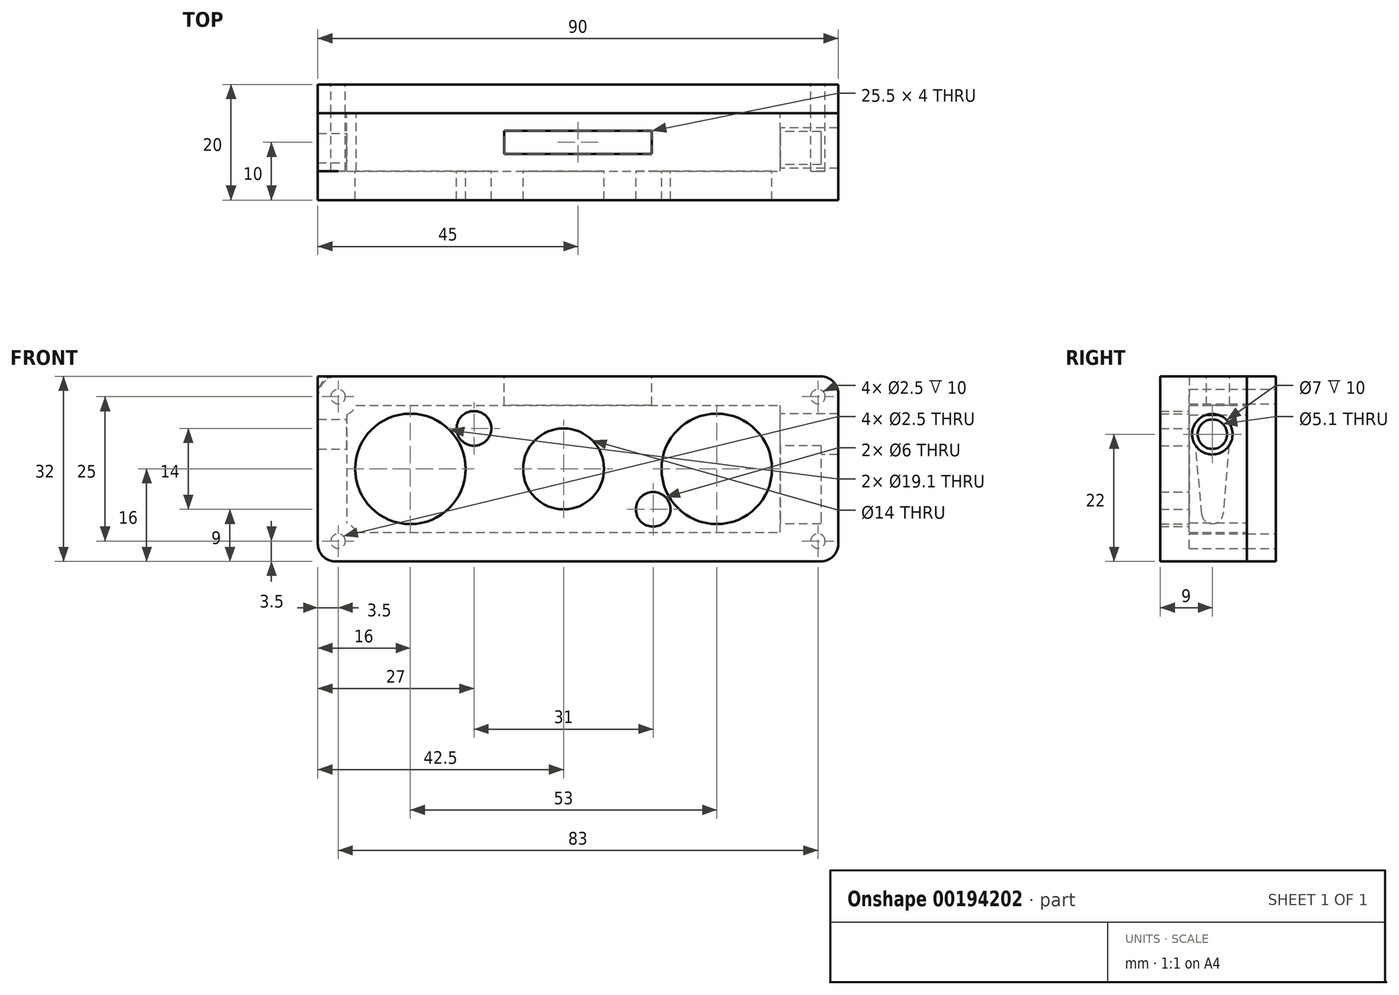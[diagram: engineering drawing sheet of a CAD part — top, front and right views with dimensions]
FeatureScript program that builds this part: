
annotation { "Feature Type Name" : "Feature", "Feature Type Description" : "" }
export const myFeature = defineFeature(function(context is Context, id is Id, definition is map)
    precondition{}
    {
        {
            var Q0;
            Q0=qCreatedBy(makeId("Front.planeOp"),FACE);
            var sketch = newSketch(context, id + "F0", { "sketchPlane" : qUnion([Q0])});
            skLineSegment(sketch, "E0.bottom", {"start": v(42.5, 16) * mm, "end": v(-42.5, 16) * mm});
            skLineSegment(sketch, "E0.top", {"start": v(42.5, -16) * mm, "end": v(-42.5, -16) * mm});
            skLineSegment(sketch, "E0.right", {"start": v(-42.5, 16) * mm, "end": v(-42.5, -16) * mm});
            skPoint(sketch, "E0.middle", {"position": v(0, 0) * mm});
            skCircle(sketch, "E1", {"center": v(-39, 12.5) * mm, "radius": 1.25 * mm});
            skCircle(sketch, "E2", {"center": v(-39, -12.5) * mm, "radius": 1.25 * mm});
            skCircle(sketch, "E3", {"center": v(44, 12.5) * mm, "radius": 1.25 * mm});
            skCircle(sketch, "E4", {"center": v(44, -12.5) * mm, "radius": 1.25 * mm});
            skLineSegment(sketch, "E5.bottom", {"start": v(42.5, 16) * mm, "end": v(47.5, 16) * mm});
            skLineSegment(sketch, "E5.top", {"start": v(42.5, -16) * mm, "end": v(47.5, -16) * mm});
            skLineSegment(sketch, "E5.right", {"start": v(47.5, 16) * mm, "end": v(47.5, -16) * mm});
            skSolve(sketch);
        }
        {
            var Q0;
            Q0=makeQuery(id+"F0.imprint","IMPRINT",FACE,{"disambiguationData":[TD([[makeQuery(id+"F0.imprint","IMPRINT",EDGE,{"derivedFrom":sQuery(id+"F0.wireOp",EDGE,"E0.bottom")}),1.0]])]});
            extrude(context, id + "F1", {"entities" : qUnion([Q0]), "depth" : 5 * mm});
        }
        {
            var Q0;
            Q0=makeQuery(id+"F1.opExtrude","CAP_FACE",FACE,{"disambiguationData":[OSD([sQuery(id+"F0.wireOp",EDGE,"E0.bottom"),sQuery(id+"F0.wireOp",EDGE,"E0.top"),sQuery(id+"F0.wireOp",EDGE,"E0.left"),sQuery(id+"F0.wireOp",EDGE,"E0.right"),sQuery(id+"F0.wireOp",EDGE,"E1"),sQuery(id+"F0.wireOp",EDGE,"E2"),sQuery(id+"F0.wireOp",EDGE,"E3"),sQuery(id+"F0.wireOp",EDGE,"E4")])],"isStart":false});
            var sketch = newSketch(context, id + "F2", { "sketchPlane" : qUnion([Q0])});
            skLineSegment(sketch, "E6.bottom", {"start": v(-42.5, 16) * mm, "end": v(42.5, 16) * mm});
            skLineSegment(sketch, "E6.top", {"start": v(-42.5, -16) * mm, "end": v(42.5, -16) * mm});
            skLineSegment(sketch, "E6.left", {"start": v(-42.5, 16) * mm, "end": v(-42.5, -16) * mm});
            skPoint(sketch, "E6.middle", {"position": v(0, 0) * mm});
            skLineSegment(sketch, "E7.bottom", {"start": v(-37.5, 11) * mm, "end": v(37.5, 11) * mm});
            skLineSegment(sketch, "E7.top", {"start": v(-37.5, -11) * mm, "end": v(37.5, -11) * mm});
            skLineSegment(sketch, "E7.left", {"start": v(-37.5, 11) * mm, "end": v(-37.5, -11) * mm});
            skCircle(sketch, "E8", {"center": v(-39, 12.5) * mm, "radius": 3.5 * mm});
            skCircle(sketch, "E9", {"center": v(-39, -12.5) * mm, "radius": 3.5 * mm});
            skCircle(sketch, "E10", {"center": v(-39, 12.5) * mm, "radius": 1.25 * mm});
            skCircle(sketch, "E11", {"center": v(-39, -12.5) * mm, "radius": 1.25 * mm});
            skCircle(sketch, "E12", {"center": v(44, -12.5) * mm, "radius": 1.25 * mm});
            skCircle(sketch, "E13", {"center": v(44, 12.5) * mm, "radius": 1.25 * mm});
            skLineSegment(sketch, "E14.bottom", {"start": v(47.5, 16) * mm, "end": v(42.5, 16) * mm});
            skLineSegment(sketch, "E14.top", {"start": v(47.5, -16) * mm, "end": v(42.5, -16) * mm});
            skLineSegment(sketch, "E14.left", {"start": v(47.5, 16) * mm, "end": v(47.5, -16) * mm});
            skLineSegment(sketch, "E15", {"start": v(37.5, -11) * mm, "end": v(37.5, 11) * mm});
            skSolve(sketch);
        }
        {
            var Q0;
            {var subQ0=sQuery(id+"F2.wireOp",EDGE,"E8");var subQ1=sQuery(id+"F2.wireOp",EDGE,"E6.left");var subQ2=makeQuery(id+"F2.imprint","INTERSECT",VERTEX,{"derivedFrom":[subQ1,subQ0]});Q0=makeQuery(id+"F2.imprint","IMPRINT",FACE,{"disambiguationData":[TD([[makeQuery(id+"F2.imprint","IMPRINT",EDGE,{"disambiguationData":[TD([[subQ2,-1.0]])],"derivedFrom":subQ1}),1.0]])]});}
            var Q1;
            Q1=makeQuery(id+"F2.imprint","IMPRINT",FACE,{"disambiguationData":[TD([[makeQuery(id+"F2.imprint","IMPRINT",EDGE,{"derivedFrom":sQuery(id+"F2.wireOp",EDGE,"E10")}),-1.0]])]});
            var Q2;
            {var subQ0=sQuery(id+"F2.wireOp",EDGE,"E6.left");var subQ1=sQuery(id+"F2.wireOp",EDGE,"E6.bottom");var subQ2=makeQuery(id+"F2.imprint","INTERSECT",VERTEX,{"derivedFrom":[subQ1,subQ0]});Q2=makeQuery(id+"F2.imprint","IMPRINT",FACE,{"disambiguationData":[TD([[makeQuery(id+"F2.imprint","IMPRINT",EDGE,{"disambiguationData":[TD([[subQ2,-1.0]])],"derivedFrom":subQ1}),-1.0]])]});}
            var Q3;
            {var subQ0=sQuery(id+"F2.wireOp",EDGE,"E6.left");var subQ1=sQuery(id+"F2.wireOp",EDGE,"E6.top");var subQ2=makeQuery(id+"F2.imprint","INTERSECT",VERTEX,{"derivedFrom":[subQ1,subQ0]});Q3=makeQuery(id+"F2.imprint","IMPRINT",FACE,{"disambiguationData":[TD([[makeQuery(id+"F2.imprint","IMPRINT",EDGE,{"disambiguationData":[TD([[subQ2,1.0]])],"derivedFrom":subQ1}),-1.0]])]});}
            var Q4;
            Q4=makeQuery(id+"F2.imprint","IMPRINT",FACE,{"disambiguationData":[TD([[makeQuery(id+"F2.imprint","IMPRINT",EDGE,{"derivedFrom":sQuery(id+"F2.wireOp",EDGE,"E11")}),-1.0]])]});
            var Q5;
            {var subQ3=sQuery(id+"F2.wireOp",EDGE,"E7.top");var subQ5=sQuery(id+"F2.wireOp",EDGE,"GZhXrjCj-0FAN-kLtT-mxsU-Lzp2gtZjm1nU.top");var subQ11=makeQuery(id+"F2.imprint","INTERSECT",VERTEX,{"derivedFrom":[subQ3,subQ5]});Q5=makeQuery(id+"F2.imprint","IMPRINT",FACE,{"disambiguationData":[TD([[makeQuery(id+"F2.imprint","IMPRINT",EDGE,{"disambiguationData":[TD([[subQ11,1.0]])],"derivedFrom":subQ3}),-1.0]])]});}
            var Q6;
            {var subQ0=sQuery(id+"F2.wireOp",EDGE,"GZhXrjCj-0FAN-kLtT-mxsU-Lzp2gtZjm1nU.top");var subQ1=sQuery(id+"F2.wireOp",EDGE,"AdWPE1ED-Ojqk-Ucqv-Uyvc-EErXh61Z168s");var subQ2=makeQuery(id+"F2.imprint","INTERSECT",VERTEX,{"derivedFrom":[subQ1,subQ0]});Q6=makeQuery(id+"F2.imprint","IMPRINT",FACE,{"disambiguationData":[TD([[makeQuery(id+"F2.imprint","IMPRINT",EDGE,{"disambiguationData":[TD([[subQ2,-1.0]])],"derivedFrom":subQ1}),1.0]])]});}
            var Q7;
            {var subQ0=sQuery(id+"F2.wireOp",EDGE,"GZhXrjCj-0FAN-kLtT-mxsU-Lzp2gtZjm1nU.right");var subQ1=sQuery(id+"F2.wireOp",EDGE,"AdWPE1ED-Ojqk-Ucqv-Uyvc-EErXh61Z168s");var subQ2=makeQuery(id+"F2.imprint","INTERSECT",VERTEX,{"derivedFrom":[subQ1,subQ0]});Q7=makeQuery(id+"F2.imprint","IMPRINT",FACE,{"disambiguationData":[TD([[makeQuery(id+"F2.imprint","IMPRINT",EDGE,{"disambiguationData":[TD([[subQ2,-1.0]])],"derivedFrom":subQ1}),1.0]])]});}
            var Q8;
            Q8=makeQuery(id+"F2.imprint","IMPRINT",FACE,{"disambiguationData":[TD([[makeQuery(id+"F2.imprint","IMPRINT",EDGE,{"derivedFrom":sQuery(id+"F2.wireOp",EDGE,"E12")}),-1.0]])]});
            var Q9;
            {var subQ0=sQuery(id+"F2.wireOp",EDGE,"E14.left");var subQ1=sQuery(id+"F2.wireOp",EDGE,"AdWPE1ED-Ojqk-Ucqv-Uyvc-EErXh61Z168s");var subQ2=makeQuery(id+"F2.imprint","INTERSECT",VERTEX,{"derivedFrom":[subQ1,subQ0]});Q9=makeQuery(id+"F2.imprint","IMPRINT",FACE,{"disambiguationData":[TD([[makeQuery(id+"F2.imprint","IMPRINT",EDGE,{"disambiguationData":[TD([[subQ2,1.0]])],"derivedFrom":subQ1}),-1.0]])]});}
            var Q10;
            {var subQ0=sQuery(id+"F2.wireOp",EDGE,"E14.top");var subQ1=sQuery(id+"F2.wireOp",EDGE,"AdWPE1ED-Ojqk-Ucqv-Uyvc-EErXh61Z168s");var subQ2=makeQuery(id+"F2.imprint","INTERSECT",VERTEX,{"derivedFrom":[subQ1,subQ0]});Q10=makeQuery(id+"F2.imprint","IMPRINT",FACE,{"disambiguationData":[TD([[makeQuery(id+"F2.imprint","IMPRINT",EDGE,{"disambiguationData":[TD([[subQ2,1.0]])],"derivedFrom":subQ1}),-1.0]])]});}
            var Q11;
            {var subQ0=sQuery(id+"F2.wireOp",EDGE,"E14.left");var subQ1=sQuery(id+"F2.wireOp",EDGE,"AdWPE1ED-Ojqk-Ucqv-Uyvc-EErXh61Z168s");var subQ2=makeQuery(id+"F2.imprint","INTERSECT",VERTEX,{"derivedFrom":[subQ1,subQ0]});Q11=makeQuery(id+"F2.imprint","IMPRINT",FACE,{"disambiguationData":[TD([[makeQuery(id+"F2.imprint","IMPRINT",EDGE,{"disambiguationData":[TD([[subQ2,-1.0]])],"derivedFrom":subQ1}),-1.0]])]});}
            var Q12;
            Q12=makeQuery(id+"F2.imprint","IMPRINT",FACE,{"disambiguationData":[TD([[makeQuery(id+"F2.imprint","IMPRINT",EDGE,{"derivedFrom":sQuery(id+"F2.wireOp",EDGE,"E13")}),-1.0]])]});
            var Q13;
            {var subQ0=sQuery(id+"F2.wireOp",EDGE,"E14.bottom");var subQ1=sQuery(id+"F2.wireOp",EDGE,"1qeEdO3c-cVBC-DGRz-gu55-AesEKtjOA0Mx");var subQ2=makeQuery(id+"F2.imprint","INTERSECT",VERTEX,{"derivedFrom":[subQ1,subQ0]});Q13=makeQuery(id+"F2.imprint","IMPRINT",FACE,{"disambiguationData":[TD([[makeQuery(id+"F2.imprint","IMPRINT",EDGE,{"disambiguationData":[TD([[subQ2,1.0]])],"derivedFrom":subQ1}),-1.0]])]});}
            var Q14;
            {var subQ0=sQuery(id+"F2.wireOp",EDGE,"E14.right");var subQ1=sQuery(id+"F2.wireOp",EDGE,"1qeEdO3c-cVBC-DGRz-gu55-AesEKtjOA0Mx");var subQ2=makeQuery(id+"F2.imprint","INTERSECT",VERTEX,{"derivedFrom":[subQ1,subQ0]});Q14=makeQuery(id+"F2.imprint","IMPRINT",FACE,{"disambiguationData":[TD([[makeQuery(id+"F2.imprint","IMPRINT",EDGE,{"disambiguationData":[TD([[subQ2,-1.0]])],"derivedFrom":subQ1}),1.0]])]});}
            var Q15;
            {var subQ0=sQuery(id+"F2.wireOp",EDGE,"GZhXrjCj-0FAN-kLtT-mxsU-Lzp2gtZjm1nU.bottom");var subQ1=sQuery(id+"F2.wireOp",EDGE,"1qeEdO3c-cVBC-DGRz-gu55-AesEKtjOA0Mx");var subQ2=makeQuery(id+"F2.imprint","INTERSECT",VERTEX,{"derivedFrom":[subQ1,subQ0]});Q15=makeQuery(id+"F2.imprint","IMPRINT",FACE,{"disambiguationData":[TD([[makeQuery(id+"F2.imprint","IMPRINT",EDGE,{"disambiguationData":[TD([[subQ2,-1.0]])],"derivedFrom":subQ1}),1.0]])]});}
            var Q16;
            {var subQ3=sQuery(id+"F2.wireOp",EDGE,"GZhXrjCj-0FAN-kLtT-mxsU-Lzp2gtZjm1nU.bottom");var subQ9=sQuery(id+"F2.wireOp",EDGE,"E7.bottom");var subQ11=makeQuery(id+"F2.imprint","INTERSECT",VERTEX,{"derivedFrom":[subQ9,subQ3]});Q16=makeQuery(id+"F2.imprint","IMPRINT",FACE,{"disambiguationData":[TD([[makeQuery(id+"F2.imprint","IMPRINT",EDGE,{"disambiguationData":[TD([[subQ11,1.0]])],"derivedFrom":subQ9}),1.0]])]});}
            var Q17;
            {var subQ0=sQuery(id+"F2.wireOp",EDGE,"E14.bottom");var subQ1=sQuery(id+"F2.wireOp",EDGE,"1qeEdO3c-cVBC-DGRz-gu55-AesEKtjOA0Mx");var subQ2=makeQuery(id+"F2.imprint","INTERSECT",VERTEX,{"derivedFrom":[subQ1,subQ0]});Q17=makeQuery(id+"F2.imprint","IMPRINT",FACE,{"disambiguationData":[TD([[makeQuery(id+"F2.imprint","IMPRINT",EDGE,{"disambiguationData":[TD([[subQ2,-1.0]])],"derivedFrom":subQ1}),-1.0]])]});}
            var Q18;
            {var subQ0=sQuery(id+"F2.wireOp",EDGE,"E7.left");var subQ1=sQuery(id+"F2.wireOp",EDGE,"E7.bottom");var subQ2=makeQuery(id+"F2.imprint","INTERSECT",VERTEX,{"derivedFrom":[subQ1,subQ0]});Q18=makeQuery(id+"F2.imprint","IMPRINT",FACE,{"disambiguationData":[TD([[makeQuery(id+"F2.imprint","IMPRINT",EDGE,{"disambiguationData":[TD([[subQ2,-1.0]])],"derivedFrom":subQ1}),-1.0]])]});}
            var Q19;
            {var subQ0=sQuery(id+"F2.wireOp",EDGE,"E7.left");var subQ1=sQuery(id+"F2.wireOp",EDGE,"E7.top");var subQ2=makeQuery(id+"F2.imprint","INTERSECT",VERTEX,{"derivedFrom":[subQ1,subQ0]});Q19=makeQuery(id+"F2.imprint","IMPRINT",FACE,{"disambiguationData":[TD([[makeQuery(id+"F2.imprint","IMPRINT",EDGE,{"disambiguationData":[TD([[subQ2,-1.0]])],"derivedFrom":subQ1}),1.0]])]});}
            extrude(context, id + "F3", {"entities" : qUnion([Q0, Q1, Q2, Q3, Q4, Q5, Q6, Q7, Q8, Q9, Q10, Q11, Q12, Q13, Q14, Q15, Q16, Q17, Q18, Q19]), "depth" : 10 * mm});
        }
        {
            var Q0;
            Q0=makeQuery(id+"F3.opExtrude","CAP_FACE",FACE,{"disambiguationData":[OSD([sQuery(id+"F2.wireOp",EDGE,"E6.bottom"),sQuery(id+"F2.wireOp",EDGE,"E6.top"),sQuery(id+"F2.wireOp",EDGE,"E6.left"),sQuery(id+"F2.wireOp",EDGE,"E6.right"),sQuery(id+"F2.wireOp",EDGE,"E7.bottom"),sQuery(id+"F2.wireOp",EDGE,"E7.top"),sQuery(id+"F2.wireOp",EDGE,"E7.left"),sQuery(id+"F2.wireOp",EDGE,"E7.right"),sQuery(id+"F2.wireOp",EDGE,"E10"),sQuery(id+"F2.wireOp",EDGE,"E11"),sQuery(id+"F2.wireOp",EDGE,"E12"),sQuery(id+"F2.wireOp",EDGE,"E13")])],"isStart":false});
            var sketch = newSketch(context, id + "F4", { "sketchPlane" : qUnion([Q0])});
            skLineSegment(sketch, "E16.bottom", {"start": v(-42.5, 16) * mm, "end": v(42.5, 16) * mm});
            skLineSegment(sketch, "E16.top", {"start": v(-42.5, -16) * mm, "end": v(42.5, -16) * mm});
            skLineSegment(sketch, "E16.left", {"start": v(-42.5, 16) * mm, "end": v(-42.5, -16) * mm});
            skPoint(sketch, "E16.middle", {"position": v(0, 0) * mm});
            skCircle(sketch, "E17", {"center": v(0, 0) * mm, "radius": 7 * mm});
            skCircle(sketch, "E18", {"center": v(26.5, 0) * mm, "radius": 9.55 * mm});
            skCircle(sketch, "E19", {"center": v(-26.5, 0) * mm, "radius": 9.55 * mm});
            skCircle(sketch, "E20", {"center": v(15.5, -7) * mm, "radius": 3 * mm});
            skCircle(sketch, "E21", {"center": v(-15.5, 7) * mm, "radius": 3 * mm});
            skLineSegment(sketch, "E22.bottom", {"start": v(42.5, 16) * mm, "end": v(47.5, 16) * mm});
            skLineSegment(sketch, "E22.top", {"start": v(42.5, -16) * mm, "end": v(47.5, -16) * mm});
            skLineSegment(sketch, "E22.right", {"start": v(47.5, 16) * mm, "end": v(47.5, -16) * mm});
            skSolve(sketch);
        }
        {
            var Q0;
            Q0 = qSketchRegion(id + "F4", true);
            extrude(context, id + "F5", {"entities" : qUnion([Q0]), "operationType" : NewBodyOperationType.ADD, "depth" : 5 * mm});
        }
        {
            var Q0;
            Q0=makeQuery(id+"F5.boolean.opBoolean","MERGE",FACE,{"derivedFrom":[makeQuery(id+"F3.opExtrude","SWEPT_FACE",FACE,{"disambiguationData":[OSD([sQuery(id+"F2.wireOp",EDGE,"E6.bottom")])]}),makeQuery(id+"F5.opExtrude","SWEPT_FACE",FACE,{"disambiguationData":[OSD([sQuery(id+"F4.wireOp",EDGE,"E16.bottom")])]})]});
            var sketch = newSketch(context, id + "F6", { "sketchPlane" : qUnion([Q0])});
            skLineSegment(sketch, "E23.bottom", {"start": v(15.25, -8) * mm, "end": v(-10.25, -8) * mm});
            skLineSegment(sketch, "E23.top", {"start": v(15.25, -12) * mm, "end": v(-10.25, -12) * mm});
            skLineSegment(sketch, "E23.left", {"start": v(15.25, -8) * mm, "end": v(15.25, -12) * mm});
            skLineSegment(sketch, "E23.right", {"start": v(-10.25, -8) * mm, "end": v(-10.25, -12) * mm});
            skPoint(sketch, "E23.middle", {"position": v(2.5, -10) * mm});
            skPoint(sketch, "E23.middle.positionSnap0", {"position": v(2.5, -20) * mm});
            skPoint(sketch, "E23.centerSnap0", {"position": v(2.5, -20) * mm});
            skSolve(sketch);
        }
        {
            var Q0;
            Q0 = qSketchRegion(id + "F6", true);
            extrude(context, id + "F7", {"entities" : qUnion([Q0]), "operationType" : NewBodyOperationType.REMOVE, "oppositeDirection" : true, "depth" : 5 * mm});
        }
        {
            var Q0;
            Q0=makeQuery(id+"F5.boolean.opBoolean","MERGE",EDGE,{"derivedFrom":[makeQuery(id+"F3.opExtrude","SWEPT_EDGE",EDGE,{"disambiguationData":[OSD([sQuery(id+"F2.wireOp",EDGE,"E14.bottom"),sQuery(id+"F2.wireOp",EDGE,"E14.left")])]}),makeQuery(id+"F5.opExtrude","SWEPT_EDGE",EDGE,{"disambiguationData":[OSD([sQuery(id+"F4.wireOp",EDGE,"E22.bottom"),sQuery(id+"F4.wireOp",EDGE,"E22.right")])]})]});
            var Q1;
            Q1=makeQuery(id+"F1.opExtrude","SWEPT_EDGE",EDGE,{"disambiguationData":[OSD([sQuery(id+"F0.wireOp",EDGE,"E5.bottom"),sQuery(id+"F0.wireOp",EDGE,"E5.right")])]});
            var Q2;
            Q2=makeQuery(id+"F1.opExtrude","SWEPT_EDGE",EDGE,{"disambiguationData":[OSD([sQuery(id+"F0.wireOp",EDGE,"E5.top"),sQuery(id+"F0.wireOp",EDGE,"E5.right")])]});
            var Q3;
            Q3=makeQuery(id+"F5.boolean.opBoolean","MERGE",EDGE,{"derivedFrom":[makeQuery(id+"F3.opExtrude","SWEPT_EDGE",EDGE,{"disambiguationData":[OSD([sQuery(id+"F2.wireOp",EDGE,"E14.top"),sQuery(id+"F2.wireOp",EDGE,"E14.left")])]}),makeQuery(id+"F5.opExtrude","SWEPT_EDGE",EDGE,{"disambiguationData":[OSD([sQuery(id+"F4.wireOp",EDGE,"E22.top"),sQuery(id+"F4.wireOp",EDGE,"E22.right")])]})]});
            var Q4;
            Q4=makeQuery(id+"F1.opExtrude","SWEPT_EDGE",EDGE,{"disambiguationData":[OSD([sQuery(id+"F0.wireOp",EDGE,"E0.bottom"),sQuery(id+"F0.wireOp",EDGE,"E0.right")])]});
            var Q5;
            Q5=makeQuery(id+"F5.boolean.opBoolean","MERGE",EDGE,{"derivedFrom":[makeQuery(id+"F3.opExtrude","SWEPT_EDGE",EDGE,{"disambiguationData":[OSD([sQuery(id+"F2.wireOp",EDGE,"E6.bottom"),sQuery(id+"F2.wireOp",EDGE,"E6.left")])]}),makeQuery(id+"F5.opExtrude","SWEPT_EDGE",EDGE,{"disambiguationData":[OSD([sQuery(id+"F4.wireOp",EDGE,"E16.bottom"),sQuery(id+"F4.wireOp",EDGE,"E16.left")])]})]});
            var Q6;
            Q6=makeQuery(id+"F1.opExtrude","SWEPT_EDGE",EDGE,{"disambiguationData":[OSD([sQuery(id+"F0.wireOp",EDGE,"E0.top"),sQuery(id+"F0.wireOp",EDGE,"E0.right")])]});
            var Q7;
            Q7=makeQuery(id+"F5.boolean.opBoolean","MERGE",EDGE,{"derivedFrom":[makeQuery(id+"F3.opExtrude","SWEPT_EDGE",EDGE,{"disambiguationData":[OSD([sQuery(id+"F2.wireOp",EDGE,"E6.top"),sQuery(id+"F2.wireOp",EDGE,"E6.left")])]}),makeQuery(id+"F5.opExtrude","SWEPT_EDGE",EDGE,{"disambiguationData":[OSD([sQuery(id+"F4.wireOp",EDGE,"E16.top"),sQuery(id+"F4.wireOp",EDGE,"E16.left")])]})]});
            fillet(context, id + "F8", {"entities" : qUnion([Q0, Q1, Q2, Q3, Q4, Q5, Q6, Q7]), "radius" : 3 * mm, "tangentPropagation" : true, "allowEdgeOverflow" : false});
        }
        {
            var Q0;
            Q0=makeQuery(id+"F3.opExtrude","SWEPT_FACE",FACE,{"disambiguationData":[OSD([sQuery(id+"F2.wireOp",EDGE,"E15")])]});
            var sketch = newSketch(context, id + "F9", { "sketchPlane" : qUnion([Q0])});
            skPoint(sketch, "E24.centerSnap0", {"position": v(10, 9.34) * mm});
            skPoint(sketch, "E25.centerSnap0", {"position": v(10, -9.34) * mm});
            skCircle(sketch, "E26", {"center": v(11, 6) * mm, "radius": 3.5 * mm});
            skCircle(sketch, "E27", {"center": v(11, -7.65) * mm, "radius": 1.85 * mm});
            skPoint(sketch, "E27.centerSnap0", {"position": v(11, -9.33) * mm});
            skLineSegment(sketch, "E28", {"start": v(12.84, -7.81) * mm, "end": v(13.88, 4.02) * mm});
            skLineSegment(sketch, "E29", {"start": v(8.12, 4.02) * mm, "end": v(9.16, -7.81) * mm});
            skLineSegment(sketch, "E30", {"start": v(9.16, -7.81) * mm, "end": v(12.84, -7.81) * mm});
            skSolve(sketch);
        }
        {
            var Q0;
            {var subQ0=sQuery(id+"F9.wireOp",EDGE,"E26");var subQ1=makeQuery(id+"F9.imprint","INTERSECT",VERTEX,{"derivedFrom":[subQ0,sQuery(id+"F9.wireOp",EDGE,"E28")]});Q0=makeQuery(id+"F9.imprint","IMPRINT",FACE,{"disambiguationData":[TD([[makeQuery(id+"F9.imprint","IMPRINT",EDGE,{"disambiguationData":[TD([[subQ1,1.0]])],"derivedFrom":subQ0}),1.0]])]});}
            extrude(context, id + "F10", {"entities" : qUnion([Q0]), "operationType" : NewBodyOperationType.REMOVE, "endBound" : BoundingType.UP_TO_NEXT, "oppositeDirection" : true, "depth" : 25 * mm});
        }
        {
            var Q0;
            Q0 = qSketchRegion(id + "F9", true);
            extrude(context, id + "F11", {"entities" : qUnion([Q0]), "operationType" : NewBodyOperationType.REMOVE, "oppositeDirection" : true, "depth" : 7 * mm});
        }
        {
            var Q0;
            Q0=sQuery(id+"F9.wireOp",VERTEX,"E26.center");
            var Q1;
            Q1=makeQuery(id+"F3.opExtrude","SWEPT_BODY",BODY,{"disambiguationData":[OSD([sQuery(id+"F2.wireOp",EDGE,"E6.bottom"),sQuery(id+"F2.wireOp",EDGE,"E6.top"),sQuery(id+"F2.wireOp",EDGE,"E6.left"),sQuery(id+"F2.wireOp",EDGE,"E7.bottom"),sQuery(id+"F2.wireOp",EDGE,"E7.top"),sQuery(id+"F2.wireOp",EDGE,"E7.left"),sQuery(id+"F2.wireOp",EDGE,"E8"),sQuery(id+"F2.wireOp",EDGE,"E9"),sQuery(id+"F2.wireOp",EDGE,"E10"),sQuery(id+"F2.wireOp",EDGE,"E11"),sQuery(id+"F2.wireOp",EDGE,"E12"),sQuery(id+"F2.wireOp",EDGE,"E13"),sQuery(id+"F2.wireOp",EDGE,"E14.bottom"),sQuery(id+"F2.wireOp",EDGE,"E14.top"),sQuery(id+"F2.wireOp",EDGE,"E14.left"),sQuery(id+"F2.wireOp",EDGE,"E15")])]});
            hole(context, id + "F12", {"style" : HoleStyle.SIMPLE, "endStyle" : HoleEndStyle.THROUGH, "oppositeDirection" : true, "holeDiameter" : 5.1 * mm, "locations" : qUnion([Q0]), "scope" : qUnion([Q1]), "isTappedThrough" : true});
        }
    });
